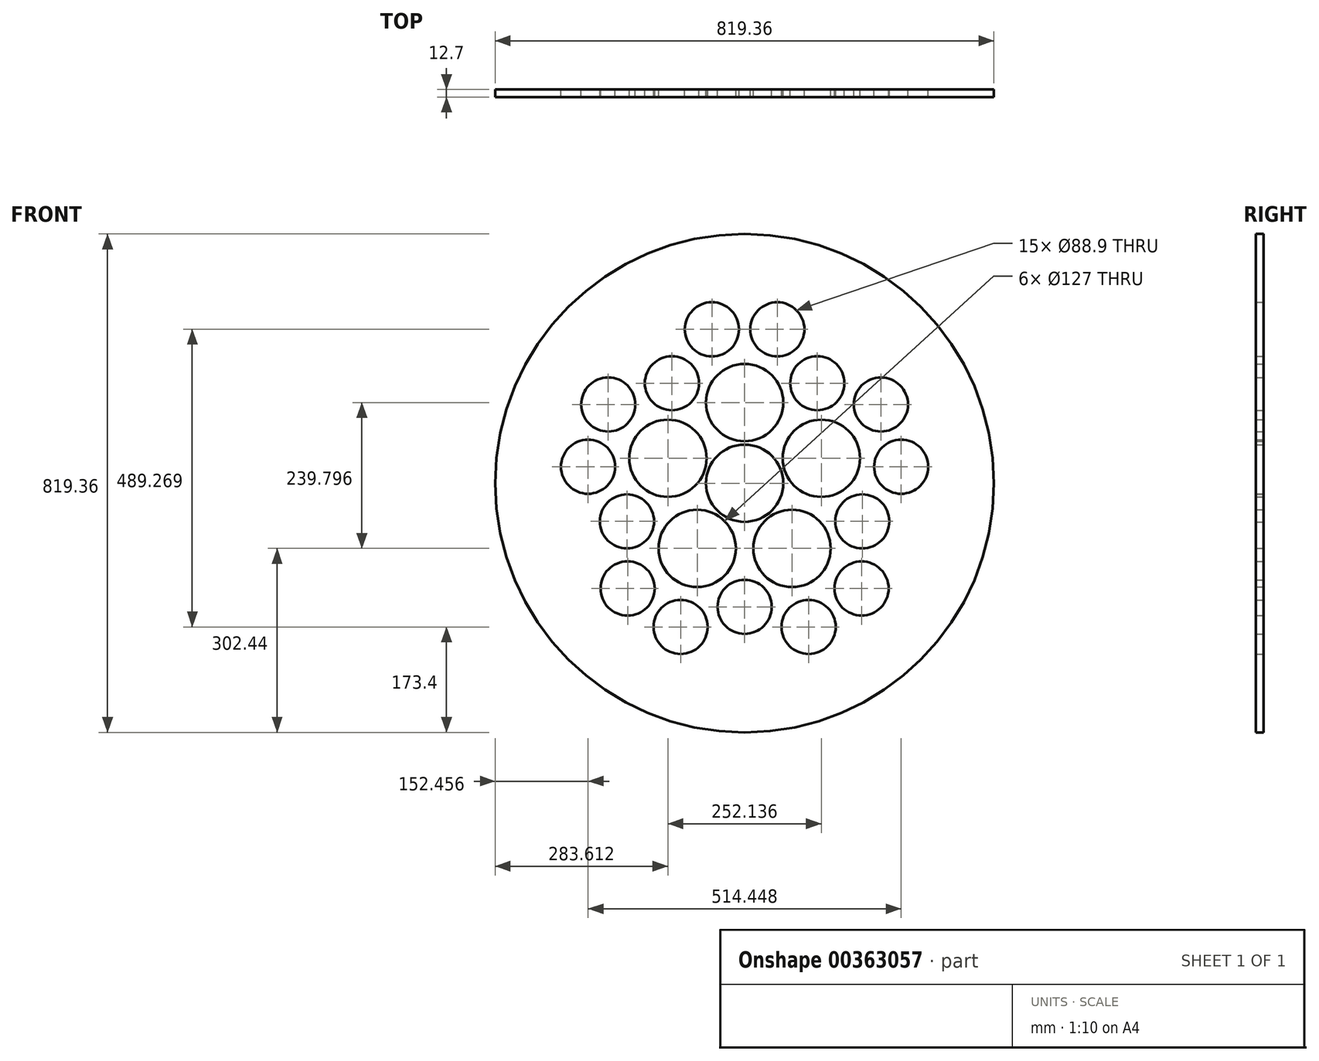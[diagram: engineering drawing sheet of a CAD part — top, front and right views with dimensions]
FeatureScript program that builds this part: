
annotation { "Feature Type Name" : "Feature", "Feature Type Description" : "" }
export const myFeature = defineFeature(function(context is Context, id is Id, definition is map)
    precondition{}
    {
        {
            var Q0;
            Q0=qCreatedBy(makeId("Front.planeOp"),FACE);
            var sketch = newSketch(context, id + "F0", { "sketchPlane" : qUnion([Q0])});
            skCircle(sketch, "E0", {"center": v(0, 0) * mm, "radius": 203.2 * mm, "construction": true});
            skCircle(sketch, "E1", {"center": v(0, 132.56) * mm, "radius": 63.5 * mm});
            skCircle(sketch, "E2.1.0", {"center": v(-126.07, 40.96) * mm, "radius": 63.5 * mm});
            skCircle(sketch, "E2.2.0", {"center": v(-77.91, -107.24) * mm, "radius": 63.5 * mm});
            skCircle(sketch, "E2.3.0", {"center": v(77.91, -107.24) * mm, "radius": 63.5 * mm});
            skCircle(sketch, "E2.4.0", {"center": v(126.07, 40.96) * mm, "radius": 63.5 * mm});
            skCircle(sketch, "E3", {"center": v(0, 0) * mm, "radius": 63.5 * mm});
            skCircle(sketch, "E4", {"center": v(0, -203.2) * mm, "radius": 44.45 * mm});
            skCircle(sketch, "E5.1.0", {"center": v(193.25, -62.8) * mm, "radius": 44.45 * mm});
            skCircle(sketch, "E5.2.0", {"center": v(119.44, 164.4) * mm, "radius": 44.45 * mm});
            skCircle(sketch, "E5.3.0", {"center": v(-119.44, 164.4) * mm, "radius": 44.45 * mm});
            skCircle(sketch, "E5.4.0", {"center": v(-193.25, -62.8) * mm, "radius": 44.45 * mm});
            skCircle(sketch, "E6", {"center": v(-105.2, -236.28) * mm, "radius": 44.45 * mm});
            skCircle(sketch, "E7", {"center": v(-192.2, -173.06) * mm, "radius": 44.45 * mm});
            skCircle(sketch, "E8", {"center": v(0, 0) * mm, "radius": 258.64 * mm, "construction": true});
            skLineSegment(sketch, "E9", {"start": v(0, 0) * mm, "end": v(-105.2, -236.28) * mm, "construction": true});
            skLineSegment(sketch, "E10", {"start": v(0, 0) * mm, "end": v(-192.2, -173.06) * mm, "construction": true});
            skLineSegment(sketch, "E11", {"start": v(0, 0) * mm, "end": v(0, -203.2) * mm, "construction": true});
            skLineSegment(sketch, "E12", {"start": v(0, 0) * mm, "end": v(-193.25, -62.8) * mm, "construction": true});
            skCircle(sketch, "E13.1.0", {"center": v(105.2, -236.28) * mm, "radius": 44.45 * mm});
            skCircle(sketch, "E13.1.1", {"center": v(192.2, -173.06) * mm, "radius": 44.45 * mm});
            skCircle(sketch, "E13.2.0", {"center": v(257.22, 27.04) * mm, "radius": 44.45 * mm});
            skCircle(sketch, "E13.2.1", {"center": v(223.99, 129.32) * mm, "radius": 44.45 * mm});
            skCircle(sketch, "E13.3.0", {"center": v(53.77, 252.99) * mm, "radius": 44.45 * mm});
            skCircle(sketch, "E13.3.1", {"center": v(-53.77, 252.99) * mm, "radius": 44.45 * mm});
            skCircle(sketch, "E13.4.0", {"center": v(-223.99, 129.32) * mm, "radius": 44.45 * mm});
            skCircle(sketch, "E13.4.1", {"center": v(-257.22, 27.04) * mm, "radius": 44.45 * mm});
            skCircle(sketch, "E14", {"center": v(0, 0) * mm, "radius": 409.68 * mm});
            skSolve(sketch);
        }
        {
            var Q0;
            Q0=makeQuery(id+"F0.imprint","IMPRINT",FACE,{"disambiguationData":[TD([[makeQuery(id+"F0.imprint","IMPRINT",EDGE,{"derivedFrom":sQuery(id+"F0.wireOp",EDGE,"E1")}),-1.0]])]});
            extrude(context, id + "F1", {"entities" : qUnion([Q0]), "depth" : 12.7 * mm, "offsetDistance" : 25.4 * mm});
        }
    });
